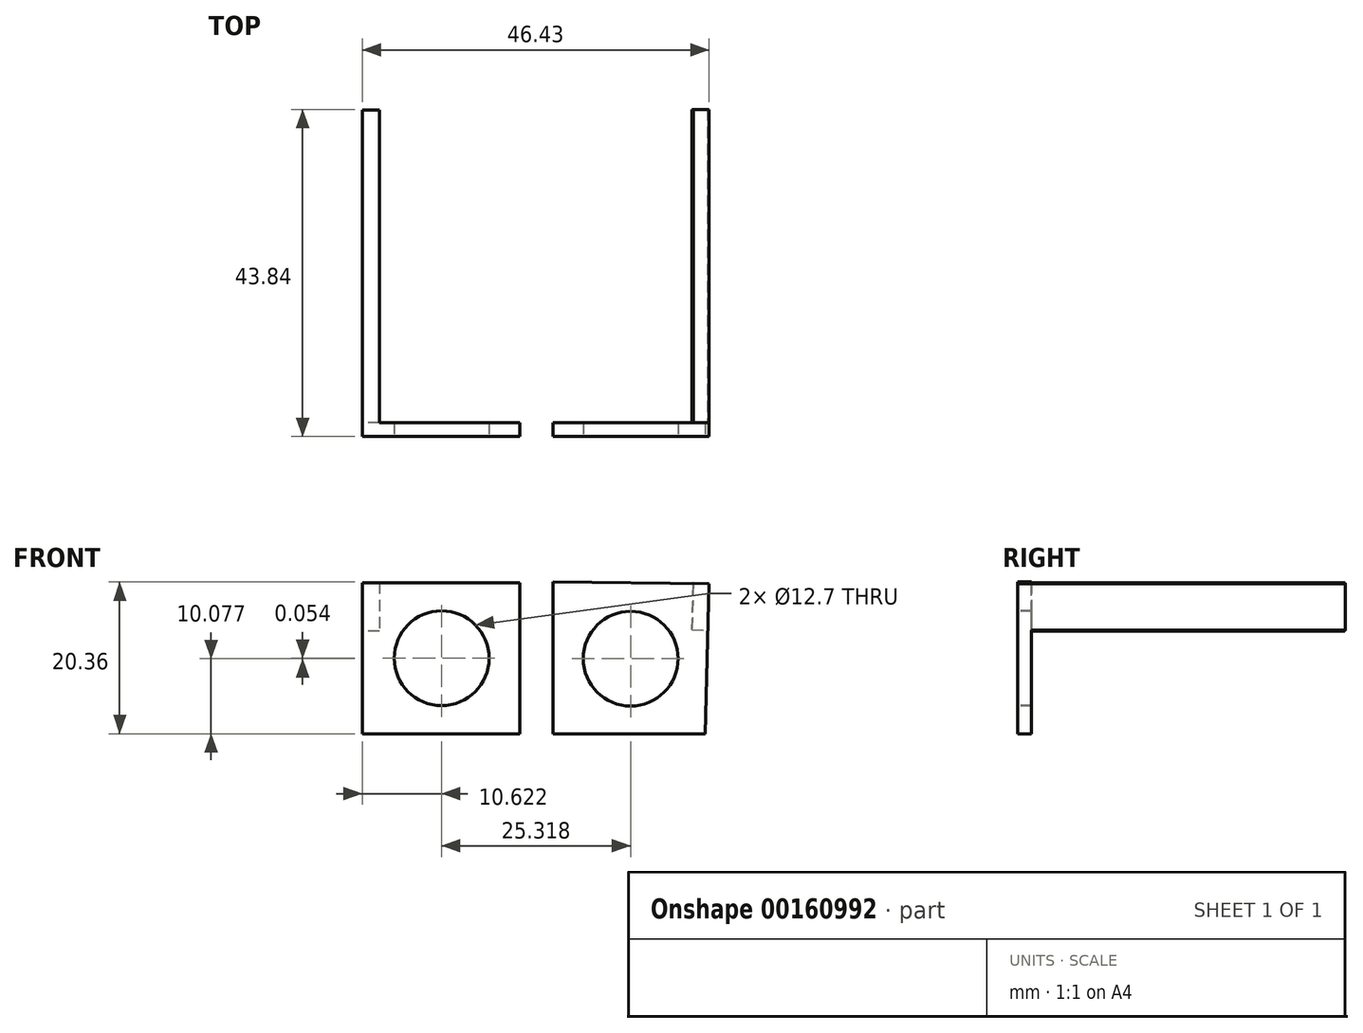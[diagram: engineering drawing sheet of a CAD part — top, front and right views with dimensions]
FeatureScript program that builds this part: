
annotation { "Feature Type Name" : "Feature", "Feature Type Description" : "" }
export const myFeature = defineFeature(function(context is Context, id is Id, definition is map)
    precondition{}
    {
        {
            var Q0;
            Q0=qCreatedBy(makeId("Front.planeOp"),FACE);
            var sketch = newSketch(context, id + "F0", { "sketchPlane" : qUnion([Q0])});
            skLineSegment(sketch, "E0", {"start": v(0, 20.26) * mm, "end": v(-21.11, 20.26) * mm});
            skLineSegment(sketch, "E1", {"start": v(-21.11, 20.26) * mm, "end": v(-21.11, 0) * mm});
            skLineSegment(sketch, "E2", {"start": v(-21.11, 0) * mm, "end": v(0, 0) * mm});
            skLineSegment(sketch, "E3", {"start": v(0, 0) * mm, "end": v(0, 20.26) * mm});
            skLineSegment(sketch, "E4", {"start": v(4.43, 20.36) * mm, "end": v(4.43, 0) * mm});
            skLineSegment(sketch, "E5", {"start": v(4.43, 0) * mm, "end": v(24.8, 0) * mm});
            skLineSegment(sketch, "E6", {"start": v(24.8, 0) * mm, "end": v(25.32, 20.13) * mm});
            skLineSegment(sketch, "E7", {"start": v(25.32, 20.13) * mm, "end": v(4.43, 20.36) * mm});
            skLineSegment(sketch, "E8", {"start": v(4.43, 20.36) * mm, "end": v(4.43, 19.68) * mm});
            skCircle(sketch, "E9", {"center": v(-10.49, 10.13) * mm, "radius": 9.74 * mm});
            skPoint(sketch, "E9.centerSnap0", {"position": v(-21.11, 10.13) * mm});
            skCircle(sketch, "E10", {"center": v(14.83, 10.08) * mm, "radius": 9.24 * mm});
            skArc(sketch, "E11", {"start": v(6.9, 0) * mm, "mid": v(2.42, 5.5) * mm, "end": v(-2.06, 0) * mm});
            skLineSegment(sketch, "E12", {"start": v(0, 20.26) * mm, "end": v(4.43, 20.36) * mm});
            skSolve(sketch);
        }
        {
            var Q0;
            Q0=makeQuery(id+"F0.imprint","IMPRINT",FACE,{"disambiguationData":[TD([[makeQuery(id+"F0.imprint","IMPRINT",EDGE,{"derivedFrom":sQuery(id+"F0.wireOp",EDGE,"E9")}),1.0]])]});
            var Q1;
            Q1=makeQuery(id+"F0.imprint","IMPRINT",FACE,{"disambiguationData":[TD([[makeQuery(id+"F0.imprint","IMPRINT",EDGE,{"derivedFrom":sQuery(id+"F0.wireOp",EDGE,"E10")}),1.0]])]});
            var Q2;
            {var subQ3=sQuery(id+"F0.wireOp",EDGE,"E0");Q2=makeQuery(id+"F0.imprint","IMPRINT",FACE,{"disambiguationData":[TD([[makeQuery(id+"F0.imprint","IMPRINT",EDGE,{"derivedFrom":subQ3}),1.0]])]});}
            var Q3;
            {var subQ0=sQuery(id+"F0.wireOp",EDGE,"SXilPgyi-9JuD-hEJO-NWPK-2iO994woBWbY");Q3=makeQuery(id+"F0.imprint","IMPRINT",FACE,{"disambiguationData":[TD([[makeQuery(id+"F0.imprint","IMPRINT",EDGE,{"derivedFrom":subQ0}),-1.0]])]});}
            var Q4;
            {var subQ3=sQuery(id+"F0.wireOp",EDGE,"9ziy6Cuv-c0mn-f5Th-dV8e-RlI7BGshgRI2");Q4=makeQuery(id+"F0.imprint","IMPRINT",FACE,{"disambiguationData":[TD([[makeQuery(id+"F0.imprint","IMPRINT",EDGE,{"derivedFrom":subQ3}),1.0]])]});}
            var Q5;
            {var subQ5=sQuery(id+"F0.wireOp",EDGE,"E8");Q5=makeQuery(id+"F0.imprint","IMPRINT",FACE,{"disambiguationData":[TD([[makeQuery(id+"F0.imprint","IMPRINT",EDGE,{"derivedFrom":subQ5}),-1.0]])]});}
            var Q6;
            {var subQ0=sQuery(id+"F0.wireOp",EDGE,"E6");Q6=makeQuery(id+"F0.imprint","IMPRINT",FACE,{"disambiguationData":[TD([[makeQuery(id+"F0.imprint","IMPRINT",EDGE,{"derivedFrom":subQ0}),1.0]])]});}
            var Q7;
            {var subQ0=sQuery(id+"F0.wireOp",EDGE,"E3");var subQ1=sQuery(id+"F0.wireOp",EDGE,"E2");var subQ2=makeQuery(id+"F0.imprint","INTERSECT",VERTEX,{"derivedFrom":[subQ1,subQ0]});Q7=makeQuery(id+"F0.imprint","IMPRINT",FACE,{"disambiguationData":[TD([[makeQuery(id+"F0.imprint","IMPRINT",EDGE,{"disambiguationData":[TD([[subQ2,1.0]])],"derivedFrom":subQ1}),1.0]])]});}
            var Q8;
            {var subQ0=sQuery(id+"F0.wireOp",EDGE,"E5");var subQ1=sQuery(id+"F0.wireOp",EDGE,"E4");var subQ2=makeQuery(id+"F0.imprint","INTERSECT",VERTEX,{"derivedFrom":[subQ1,subQ0]});Q8=makeQuery(id+"F0.imprint","IMPRINT",FACE,{"disambiguationData":[TD([[makeQuery(id+"F0.imprint","IMPRINT",EDGE,{"disambiguationData":[TD([[subQ2,1.0]])],"derivedFrom":subQ1}),1.0]])]});}
            extrude(context, id + "F1", {"entities" : qUnion([Q0, Q1, Q2, Q3, Q4, Q5, Q6, Q7, Q8]), "oppositeDirection" : true, "depth" : 1.84 * mm});
        }
        {
            var Q0;
            Q0=sQuery(id+"F0.wireOp",VERTEX,"E9.center");
            var Q1;
            Q1=sQuery(id+"F0.wireOp",VERTEX,"E10.center");
            var Q2;
            Q2=makeQuery(id+"F1.opExtrude","SWEPT_BODY",BODY,{"disambiguationData":[OSD([sQuery(id+"F0.wireOp",EDGE,"E0"),sQuery(id+"F0.wireOp",EDGE,"E1"),sQuery(id+"F0.wireOp",EDGE,"E2"),sQuery(id+"F0.wireOp",EDGE,"E3"),sQuery(id+"F0.wireOp",EDGE,"E4"),sQuery(id+"F0.wireOp",EDGE,"E5"),sQuery(id+"F0.wireOp",EDGE,"E6"),sQuery(id+"F0.wireOp",EDGE,"E7"),sQuery(id+"F0.wireOp",EDGE,"E11"),sQuery(id+"F0.wireOp",EDGE,"E12")])]});
            hole(context, id + "F2", {"style" : HoleStyle.SIMPLE, "endStyle" : HoleEndStyle.THROUGH, "holeDiameter" : 12.7 * mm, "locations" : qUnion([Q0, Q1]), "scope" : qUnion([Q2]), "isTappedThrough" : true});
        }
        {
            var Q0;
            Q0=makeQuery(id+"F1.opExtrude","SWEPT_FACE",FACE,{"disambiguationData":[OSD([sQuery(id+"F0.wireOp",EDGE,"E6")])]});
            var sketch = newSketch(context, id + "F3", { "sketchPlane" : qUnion([Q0])});
            skLineSegment(sketch, "E13", {"start": v(0, 20.78) * mm, "end": v(43.84, 20.78) * mm});
            skPoint(sketch, "E13.endSnap0", {"position": v(0.92, 20.78) * mm});
            skLineSegment(sketch, "E14", {"start": v(43.84, 20.78) * mm, "end": v(43.84, 14.55) * mm});
            skLineSegment(sketch, "E15", {"start": v(43.84, 14.55) * mm, "end": v(0, 14.55) * mm});
            skLineSegment(sketch, "E16", {"start": v(0, 20.78) * mm, "end": v(0, 14.55) * mm});
            skSolve(sketch);
        }
        {
            var Q0;
            Q0=makeQuery(id+"F1.opExtrude","SWEPT_FACE",FACE,{"disambiguationData":[OSD([sQuery(id+"F0.wireOp",EDGE,"E1")])]});
            var sketch = newSketch(context, id + "F4", { "sketchPlane" : qUnion([Q0])});
            skLineSegment(sketch, "E17", {"start": v(0, 20.26) * mm, "end": v(-43.77, 20.26) * mm});
            skLineSegment(sketch, "E18", {"start": v(-43.77, 20.26) * mm, "end": v(-43.77, 13.78) * mm});
            skLineSegment(sketch, "E19", {"start": v(-43.77, 13.78) * mm, "end": v(0, 13.78) * mm});
            skSolve(sketch);
        }
        {
            var Q0;
            {var subQ3=sQuery(id+"F4.wireOp",EDGE,"E18");Q0=makeQuery(id+"F4.imprint","IMPRINT",FACE,{"disambiguationData":[TD([[makeQuery(id+"F4.imprint","IMPRINT",EDGE,{"derivedFrom":subQ3}),1.0]])]});}
            extrude(context, id + "F5", {"entities" : qUnion([Q0]), "operationType" : NewBodyOperationType.ADD, "oppositeDirection" : true, "depth" : 2.3 * mm});
        }
        {
            var Q0;
            {var subQ3=sQuery(id+"F3.wireOp",EDGE,"E14");Q0=makeQuery(id+"F3.imprint","IMPRINT",FACE,{"disambiguationData":[TD([[makeQuery(id+"F3.imprint","IMPRINT",EDGE,{"derivedFrom":subQ3}),-1.0]])]});}
            extrude(context, id + "F6", {"entities" : qUnion([Q0]), "operationType" : NewBodyOperationType.ADD, "oppositeDirection" : true, "depth" : 2.1 * mm});
        }
    });
